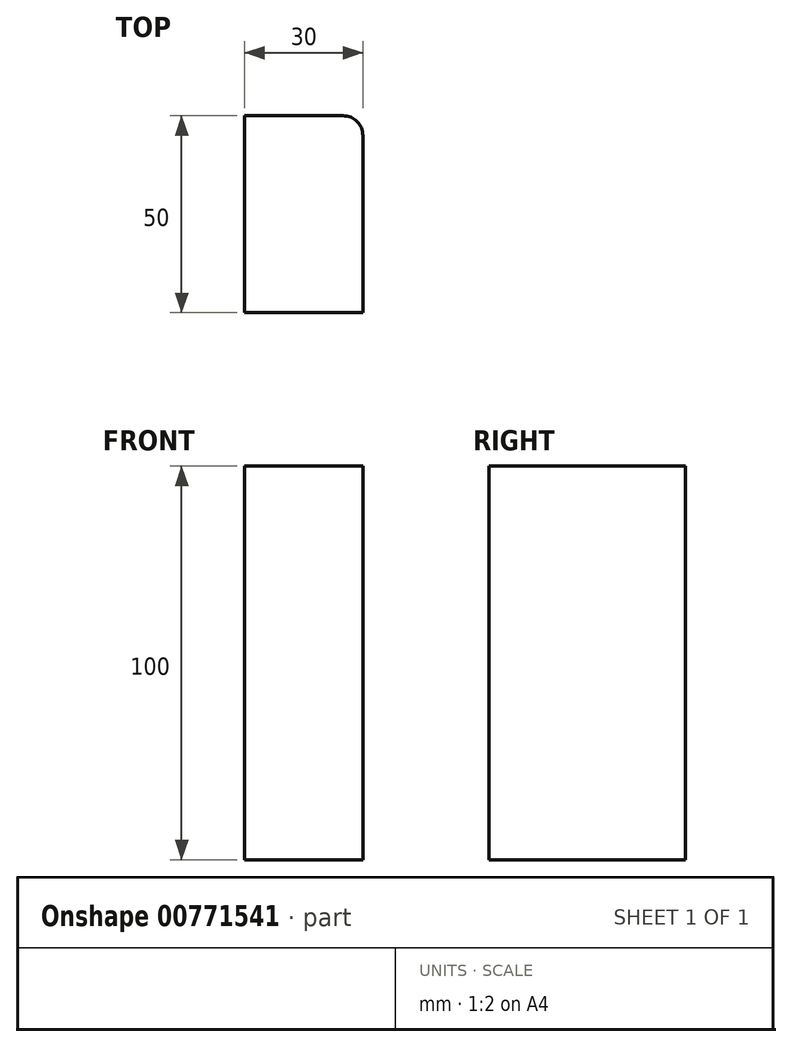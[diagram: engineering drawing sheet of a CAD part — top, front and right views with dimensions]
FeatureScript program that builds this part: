
annotation { "Feature Type Name" : "Feature", "Feature Type Description" : "" }
export const myFeature = defineFeature(function(context is Context, id is Id, definition is map)
    precondition{}
    {
        {
            var Q0;
            Q0=qCreatedBy(makeId("Top.planeOp"),FACE);
            var sketch = newSketch(context, id + "F0", { "sketchPlane" : qUnion([Q0])});
            skLineSegment(sketch, "E0.bottom", {"start": v(15, 25) * mm, "end": v(-15, 25) * mm});
            skLineSegment(sketch, "E0.top", {"start": v(15, -25) * mm, "end": v(-15, -25) * mm});
            skLineSegment(sketch, "E0.left", {"start": v(15, 25) * mm, "end": v(15, -25) * mm});
            skLineSegment(sketch, "E0.right", {"start": v(-15, 25) * mm, "end": v(-15, -25) * mm});
            skPoint(sketch, "E0.middle", {"position": v(0, 0) * mm});
            skSolve(sketch);
        }
        {
            var Q0;
            Q0=makeQuery(id+"F0.imprint","IMPRINT",FACE,{"disambiguationData":[TD([[makeQuery(id+"F0.imprint","IMPRINT",EDGE,{"derivedFrom":sQuery(id+"F0.wireOp",EDGE,"E0.bottom")}),1.0]])]});
            extrude(context, id + "F1", {"entities" : qUnion([Q0]), "depth" : 100 * mm, "offsetDistance" : 25 * mm});
        }
        {
            var Q0;
            Q0=makeQuery(id+"F1.opExtrude","SWEPT_EDGE",EDGE,{"disambiguationData":[OSD([sQuery(id+"F0.wireOp",EDGE,"E0.bottom"),sQuery(id+"F0.wireOp",EDGE,"E0.left")])]});
            fillet(context, id + "F2", {"entities" : qUnion([Q0]), "radius" : 5 * mm, "tangentPropagation" : true, "allowEdgeOverflow" : false});
        }
    });
